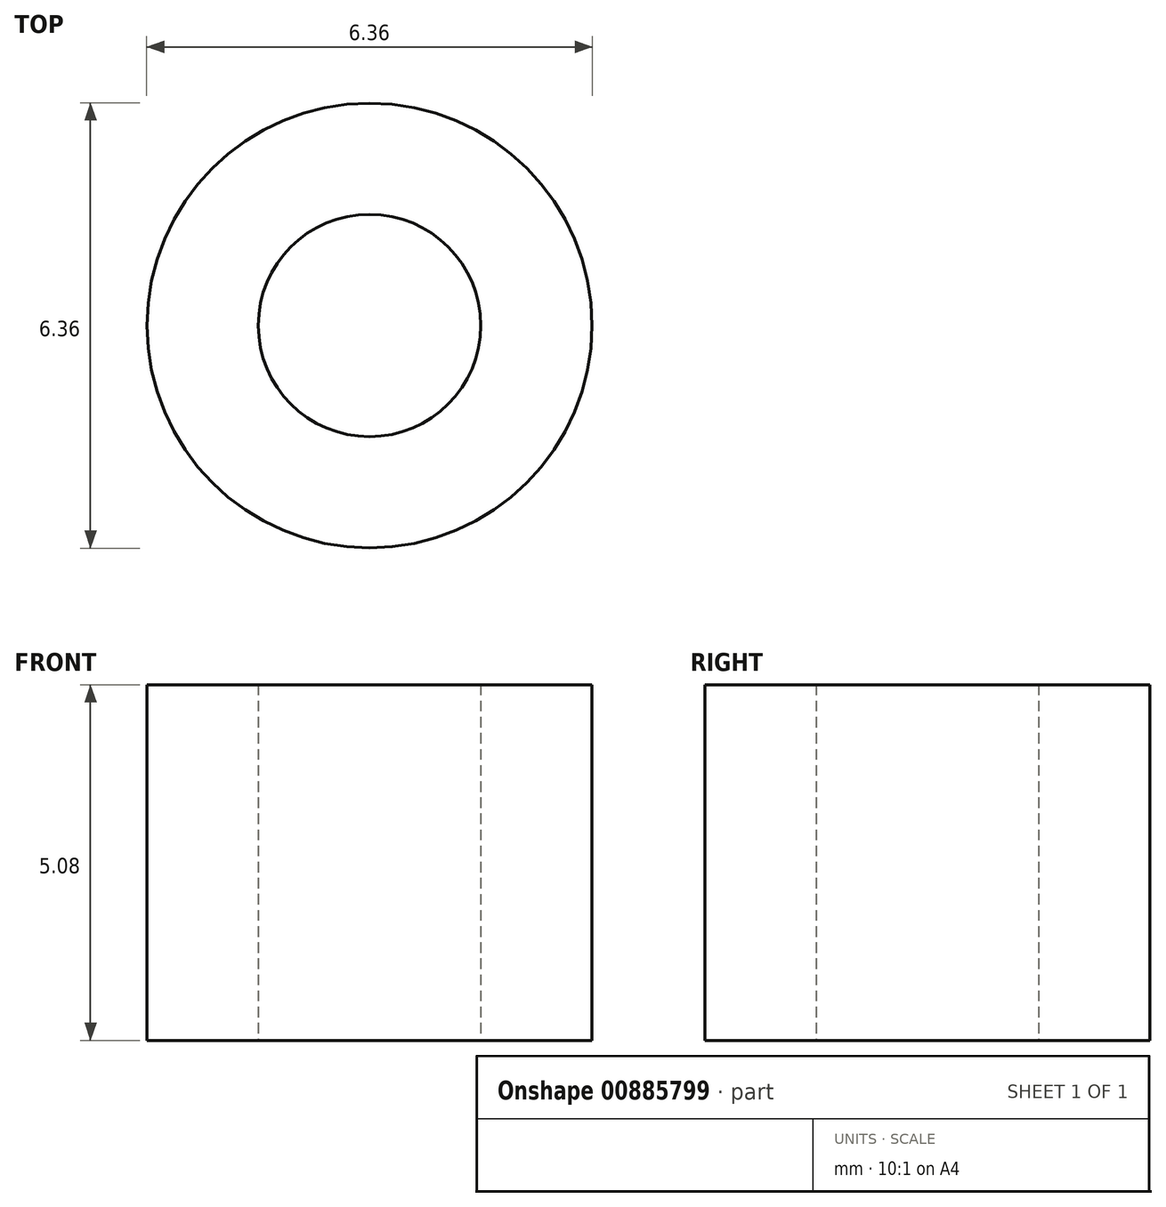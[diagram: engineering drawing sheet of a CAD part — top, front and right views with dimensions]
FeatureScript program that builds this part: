
annotation { "Feature Type Name" : "Feature", "Feature Type Description" : "" }
export const myFeature = defineFeature(function(context is Context, id is Id, definition is map)
    precondition{}
    {
        {
            var Q0;
            Q0=qCreatedBy(makeId("Top.planeOp"),FACE);
            var sketch = newSketch(context, id + "F0", { "sketchPlane" : qUnion([Q0])});
            skCircle(sketch, "E0", {"center": v(0, 0) * mm, "radius": 1.59 * mm});
            skCircle(sketch, "E1", {"center": v(0, 0) * mm, "radius": 3.18 * mm});
            skSolve(sketch);
        }
        {
            var Q0;
            Q0 = qSketchRegion(id + "F0", true);
            extrude(context, id + "F1", {"entities" : qUnion([Q0]), "depth" : 5.08 * mm, "offsetDistance" : 25.4 * mm});
        }
    });
